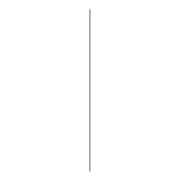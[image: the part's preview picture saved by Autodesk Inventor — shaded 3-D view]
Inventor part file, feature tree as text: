
AUTODESK INVENTOR PART (.ipt)
format: ipt  version: 2022 (Build 260153000, 153)  size: 75,776 bytes
history: native  units: mm
features: extrude x1, sketch x1
ambient origin geometry x8: Origin, YZ Plane, XZ Plane, XY Plane, X Axis, Y Axis, Z Axis, Center Point
bodies: Solid1 (feature_tree)
feature tree (2):
  extrude  "Extrusion1"  Depth=500.0mm TaperAngle=0.0deg
  sketch  "Sketch1"  dims[d0=5.35mm d1=500.0mm d2=0.0mm d3=3.2mm]
